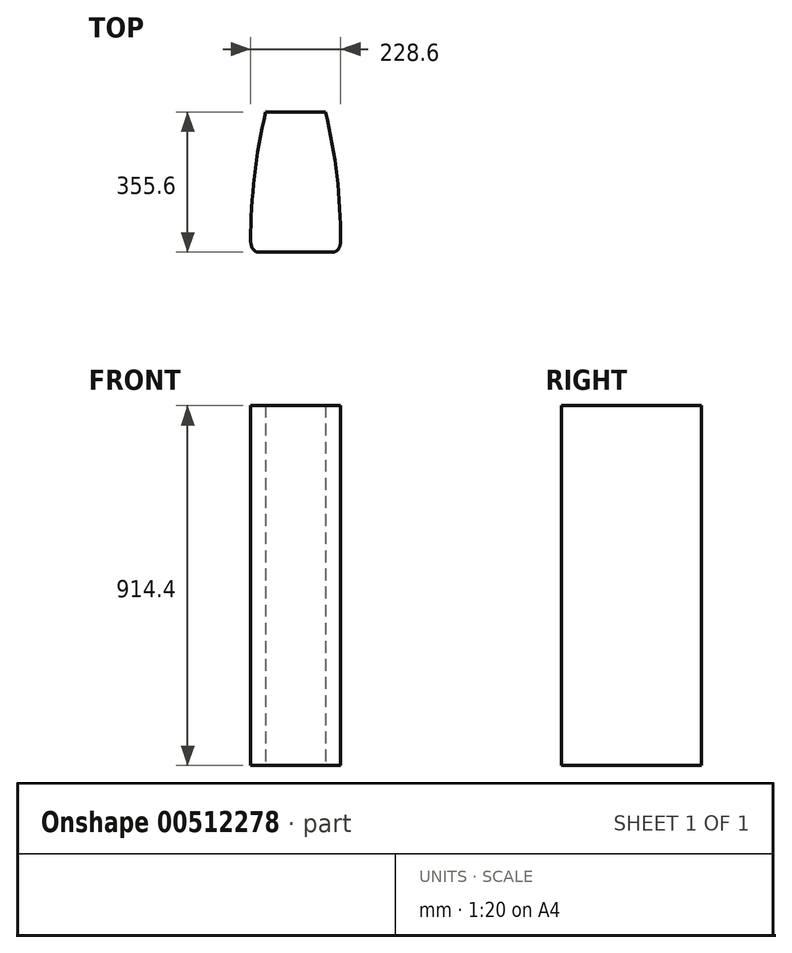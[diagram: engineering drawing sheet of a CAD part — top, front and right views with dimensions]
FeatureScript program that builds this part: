
annotation { "Feature Type Name" : "Feature", "Feature Type Description" : "" }
export const myFeature = defineFeature(function(context is Context, id is Id, definition is map)
    precondition{}
    {
        {
            var Q0;
            Q0=qCreatedBy(makeId("Top.planeOp"),FACE);
            var sketch = newSketch(context, id + "F0", { "sketchPlane" : qUnion([Q0])});
            skArc(sketch, "E0", {"start": v(-76.2, 355.6) * mm, "mid": v(-106.33, 179) * mm, "end": v(-114.01, 0) * mm});
            skArc(sketch, "E1", {"start": v(114.01, 0) * mm, "mid": v(106.33, 179) * mm, "end": v(76.2, 355.6) * mm});
            skLineSegment(sketch, "E2", {"start": v(-76.2, 355.6) * mm, "end": v(76.2, 355.6) * mm});
            skLineSegment(sketch, "E3", {"start": v(-114.01, 0) * mm, "end": v(114.01, 0) * mm});
            skEllipse(sketch, "E4", {"center": v(-95.25, 28.58) * mm, "majorRadius": 28.58 * mm, "minorRadius": 19.05 * mm, "majorAxis": v(0, 1)});
            skEllipse(sketch, "E5", {"center": v(95.25, 28.58) * mm, "majorRadius": 28.58 * mm, "minorRadius": 19.05 * mm, "majorAxis": v(0, 1)});
            skSolve(sketch);
        }
        {
            var Q0;
            {var subQ5=sQuery(id+"F0.wireOp",EDGE,"E2");Q0=makeQuery(id+"F0.imprint","IMPRINT",FACE,{"disambiguationData":[TD([[makeQuery(id+"F0.imprint","IMPRINT",EDGE,{"derivedFrom":subQ5}),-1.0]])]});}
            var Q1;
            {var subQ0=sQuery(id+"F0.wireOp",EDGE,"E4");var subQ1=makeQuery(id+"F0.imprint","INTERSECT",VERTEX,{"derivedFrom":[sQuery(id+"F0.wireOp",EDGE,"E0"),subQ0]});Q1=makeQuery(id+"F0.imprint","IMPRINT",FACE,{"disambiguationData":[TD([[makeQuery(id+"F0.imprint","IMPRINT",EDGE,{"disambiguationData":[TD([[subQ1,-1.0]])],"derivedFrom":subQ0}),1.0]])]});}
            var Q2;
            {var subQ0=sQuery(id+"F0.wireOp",EDGE,"E5");var subQ1=makeQuery(id+"F0.imprint","INTERSECT",VERTEX,{"derivedFrom":[sQuery(id+"F0.wireOp",EDGE,"E1"),subQ0]});Q2=makeQuery(id+"F0.imprint","IMPRINT",FACE,{"disambiguationData":[TD([[makeQuery(id+"F0.imprint","IMPRINT",EDGE,{"disambiguationData":[TD([[subQ1,1.0]])],"derivedFrom":subQ0}),1.0]])]});}
            extrude(context, id + "F1", {"entities" : qUnion([Q0, Q1, Q2]), "depth" : 914.4 * mm});
        }
    });
